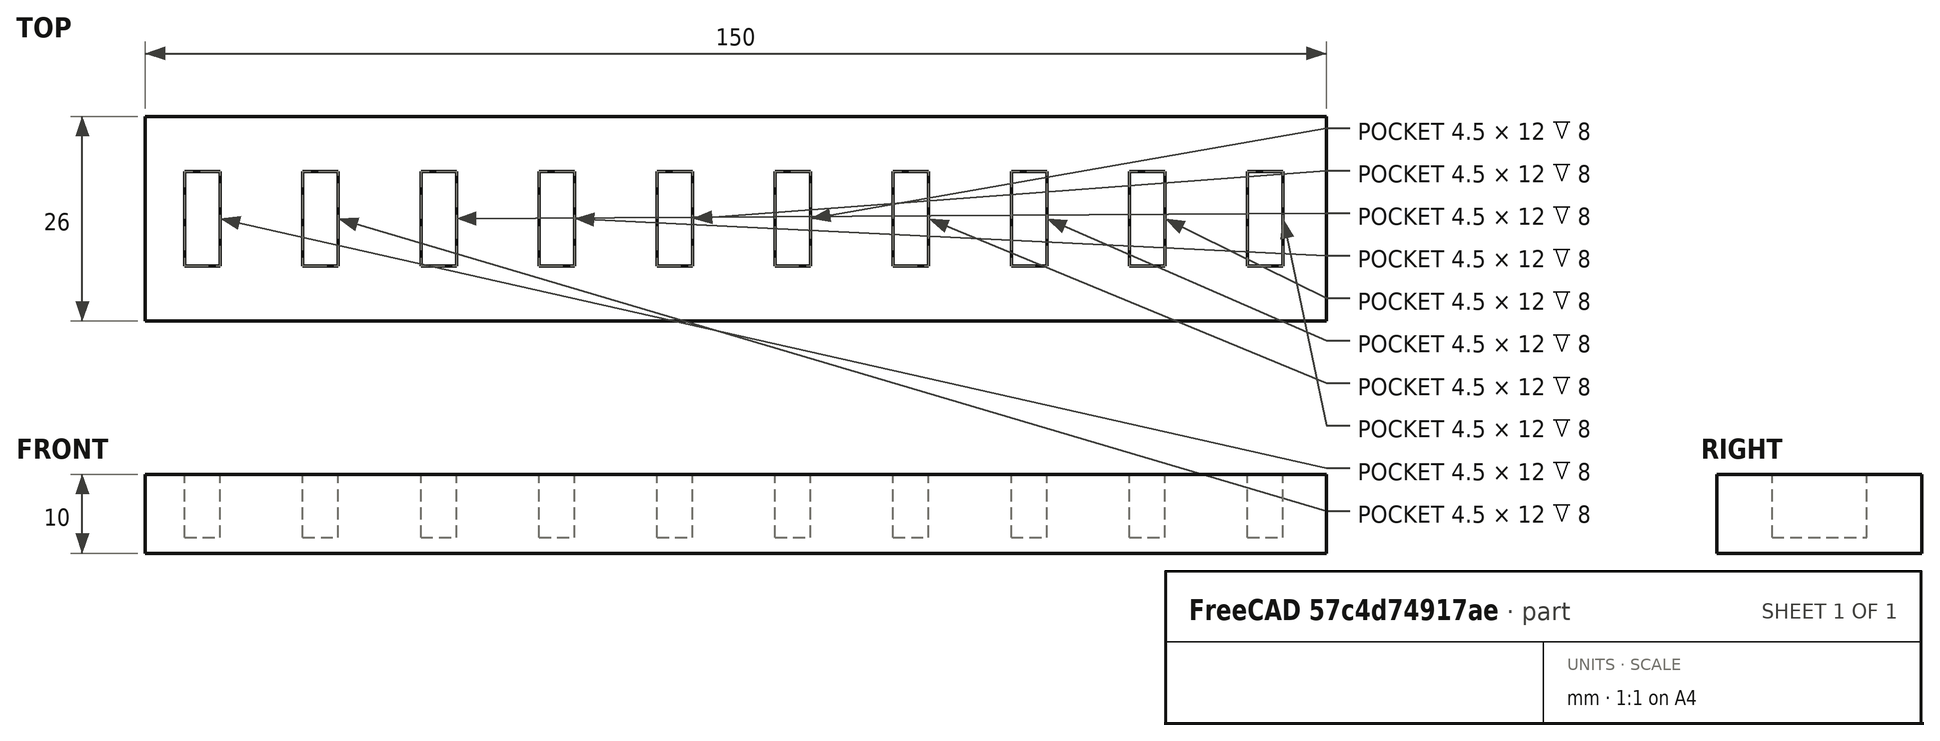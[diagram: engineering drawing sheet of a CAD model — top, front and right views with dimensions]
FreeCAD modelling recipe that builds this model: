
FCSTD DOCUMENT  (FreeCAD 0.16R6707 (Git))
Label: 07-portapendrives-parametrico
License: All rights reserved
LicenseURL: http://en.wikipedia.org/wiki/All_rights_reserved
objects: Part::Box×2, Spreadsheet::Sheet×1, Part::FeaturePython×1, Part::Cut×1
note: 4 computed .brp shape members not serialized (recipe doc carries the construction recipe); baked Part::Feature solids carry a one-line shape summary decoded from their .brp

FEATURE [Spreadsheet::Sheet] Spreadsheet  label="Parametros"
  cells = B3=n: Numero de pendrives; C3(n)=10; B4=d: Distancia entre pendrives; C4(d)=15
FEATURE [Part::Box] Box001  label="Cubo001"
  Height = 15
  Length = 4.5
  Placement = pos=(5,7,2) rot=(0,0,1;0rad)
  Width = 12
  expr: Placement.Base.x = Parametros.d / 3
FEATURE [Part::FeaturePython] Array  # Draft array (typed FeaturePython)
  Angle = 360
  ArrayType = 0
  Axis = (0,0,1)
  Base = -> Box001
  Center = (0,0,0)
  Fuse = false
  IntervalAxis = (0,0,0)
  IntervalX = (15,0,0)
  IntervalY = (0,1,0)
  IntervalZ = (0,0,0)
  NumberPolar = 1
  NumberX = 10
  NumberY = 1
  NumberZ = 1
  expr: IntervalX.x = Parametros.d
  expr: NumberX = Parametros.n
FEATURE [Part::Box] Box  label="Base"
  Height = 10
  Length = 150
  Width = 26
  expr: Length = Parametros.d * Parametros.n
FEATURE [Part::Cut] Cut
  Base = -> Box
  Tool = -> Array
